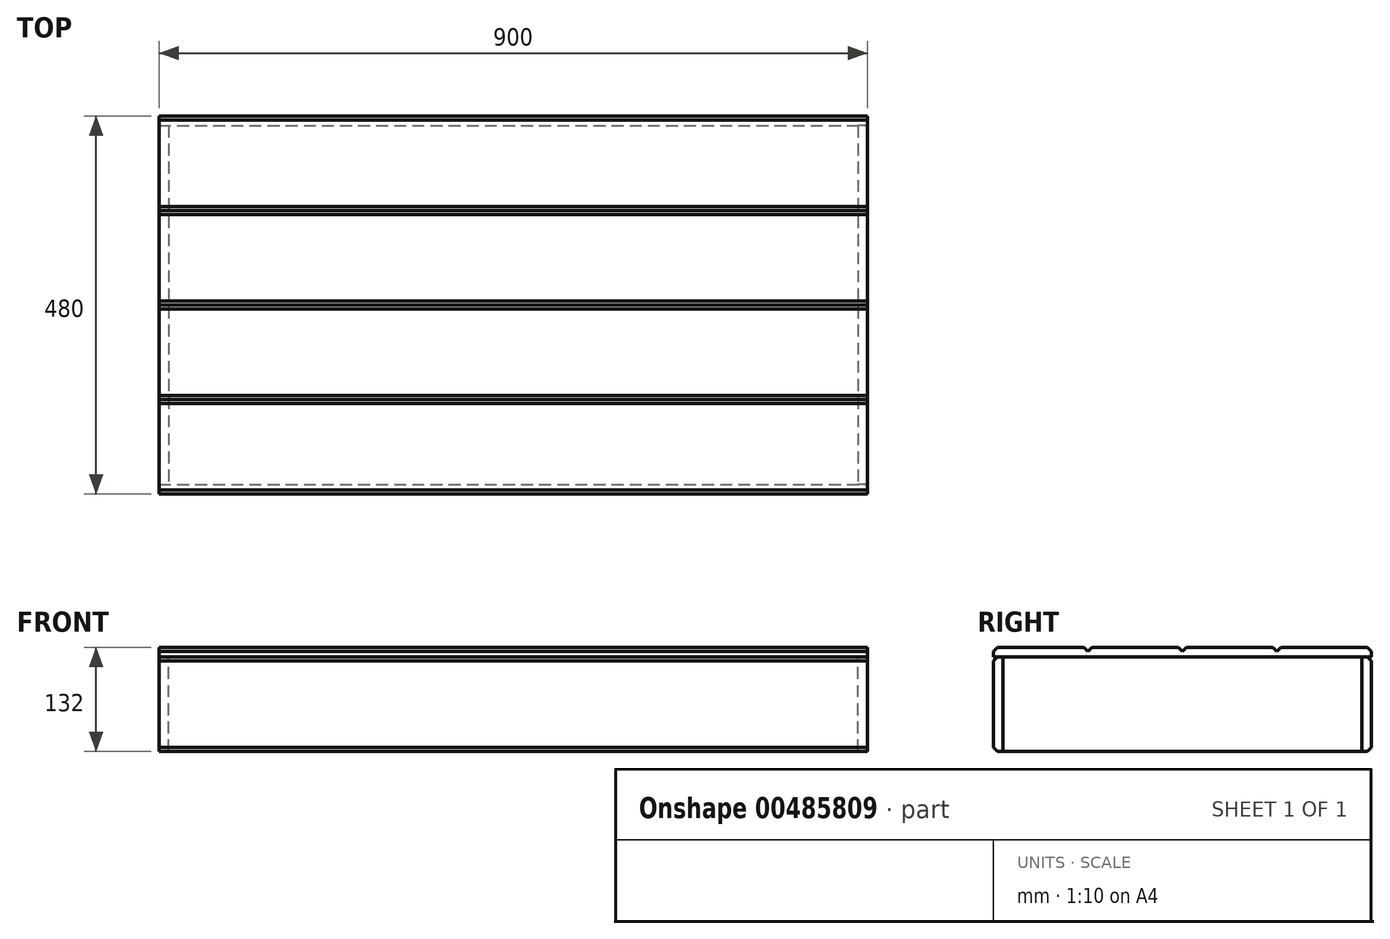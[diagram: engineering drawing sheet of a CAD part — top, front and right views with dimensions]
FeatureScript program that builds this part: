
annotation { "Feature Type Name" : "Feature", "Feature Type Description" : "" }
export const myFeature = defineFeature(function(context is Context, id is Id, definition is map)
    precondition{}
    {
        {
            var Q0;
            Q0=qCreatedBy(makeId("Top.planeOp"),FACE);
            var sketch = newSketch(context, id + "F0", { "sketchPlane" : qUnion([Q0])});
            skLineSegment(sketch, "E0", {"start": v(-56.43, 473.78) * mm, "end": v(-56.43, -6.22) * mm});
            skLineSegment(sketch, "E1", {"start": v(-56.43, -6.22) * mm, "end": v(843.57, -6.22) * mm});
            skLineSegment(sketch, "E2", {"start": v(-56.43, 473.78) * mm, "end": v(843.57, 473.78) * mm});
            skLineSegment(sketch, "E3", {"start": v(843.57, 473.78) * mm, "end": v(843.57, -6.22) * mm});
            skSolve(sketch);
        }
        {
            var Q0;
            Q0=makeQuery(id+"F0.imprint","IMPRINT",FACE,{"disambiguationData":[TD([[makeQuery(id+"F0.imprint","IMPRINT",EDGE,{"derivedFrom":sQuery(id+"F0.wireOp",EDGE,"E0")}),1.0]])]});
            extrude(context, id + "F1", {"entities" : qUnion([Q0]), "depth" : 12 * mm});
        }
        {
            var Q0;
            Q0=makeQuery(id+"F1.opExtrude","SWEPT_FACE",FACE,{"disambiguationData":[OSD([sQuery(id+"F0.wireOp",EDGE,"E3")])]});
            var sketch = newSketch(context, id + "F2", { "sketchPlane" : qUnion([Q0])});
            skLineSegment(sketch, "E4", {"start": v(-6.22, 12) * mm, "end": v(-1.22, 12) * mm});
            skLineSegment(sketch, "E5", {"start": v(-1.22, 12) * mm, "end": v(-6.22, 7) * mm});
            skLineSegment(sketch, "E6", {"start": v(-6.22, 7) * mm, "end": v(-6.22, 12) * mm});
            skLineSegment(sketch, "E7", {"start": v(-6.22, 18.21) * mm, "end": v(113.78, 18.21) * mm, "construction": true});
            skLineSegment(sketch, "E8", {"start": v(113.78, 12) * mm, "end": v(108.78, 12) * mm});
            skLineSegment(sketch, "E9", {"start": v(108.78, 12) * mm, "end": v(113.78, 7) * mm});
            skLineSegment(sketch, "E10", {"start": v(113.78, 7) * mm, "end": v(118.78, 12) * mm});
            skLineSegment(sketch, "E11", {"start": v(118.78, 12) * mm, "end": v(113.78, 12) * mm});
            skLineSegment(sketch, "E12", {"start": v(113.78, 18.21) * mm, "end": v(233.78, 18.21) * mm, "construction": true});
            skLineSegment(sketch, "E13", {"start": v(233.78, 18.21) * mm, "end": v(353.78, 18.21) * mm, "construction": true});
            skLineSegment(sketch, "E14", {"start": v(353.78, 18.21) * mm, "end": v(473.78, 18.21) * mm, "construction": true});
            skLineSegment(sketch, "E15", {"start": v(233.78, 12) * mm, "end": v(228.78, 12) * mm});
            skLineSegment(sketch, "E16", {"start": v(228.78, 12) * mm, "end": v(233.78, 7) * mm});
            skLineSegment(sketch, "E17", {"start": v(233.78, 7) * mm, "end": v(238.78, 12) * mm});
            skLineSegment(sketch, "E18", {"start": v(238.78, 12) * mm, "end": v(233.78, 12) * mm});
            skLineSegment(sketch, "E19", {"start": v(353.78, 12) * mm, "end": v(348.78, 12) * mm});
            skLineSegment(sketch, "E20", {"start": v(348.78, 12) * mm, "end": v(353.78, 7) * mm});
            skLineSegment(sketch, "E21", {"start": v(353.78, 7) * mm, "end": v(358.78, 12) * mm});
            skLineSegment(sketch, "E22", {"start": v(358.78, 12) * mm, "end": v(353.78, 12) * mm});
            skLineSegment(sketch, "E23", {"start": v(473.78, 12) * mm, "end": v(468.78, 12) * mm});
            skLineSegment(sketch, "E24", {"start": v(473.78, 12) * mm, "end": v(473.78, 7) * mm});
            skLineSegment(sketch, "E25", {"start": v(473.78, 7) * mm, "end": v(468.78, 12) * mm});
            skSolve(sketch);
        }
        {
            var Q0;
            Q0 = qSketchRegion(id + "F2", true);
            extrude(context, id + "F3", {"entities" : qUnion([Q0]), "operationType" : NewBodyOperationType.REMOVE, "endBound" : BoundingType.THROUGH_ALL, "oppositeDirection" : true, "depth" : 900 * mm});
        }
        {
            var Q0;
            Q0=makeQuery(id+"F1.opExtrude","CAP_FACE",FACE,{"disambiguationData":[OSD([sQuery(id+"F0.wireOp",EDGE,"E0"),sQuery(id+"F0.wireOp",EDGE,"E1"),sQuery(id+"F0.wireOp",EDGE,"E2"),sQuery(id+"F0.wireOp",EDGE,"E3")])],"isStart":true});
            var sketch = newSketch(context, id + "F4", { "sketchPlane" : qUnion([Q0])});
            skLineSegment(sketch, "E26.bottom", {"start": v(-56.43, -473.78) * mm, "end": v(843.57, -473.78) * mm});
            skLineSegment(sketch, "E26.top", {"start": v(-56.43, -461.78) * mm, "end": v(843.57, -461.78) * mm});
            skLineSegment(sketch, "E26.left", {"start": v(-56.43, -473.78) * mm, "end": v(-56.43, -461.78) * mm});
            skLineSegment(sketch, "E26.right", {"start": v(843.57, -473.78) * mm, "end": v(843.57, -461.78) * mm});
            skSolve(sketch);
        }
        {
            var Q0;
            Q0 = qSketchRegion(id + "F4", true);
            extrude(context, id + "F5", {"entities" : qUnion([Q0]), "depth" : 120 * mm});
        }
        {
            var Q0;
            Q0=makeQuery(id+"F1.opExtrude","CAP_FACE",FACE,{"disambiguationData":[OSD([sQuery(id+"F0.wireOp",EDGE,"E0"),sQuery(id+"F0.wireOp",EDGE,"E1"),sQuery(id+"F0.wireOp",EDGE,"E2"),sQuery(id+"F0.wireOp",EDGE,"E3")])],"isStart":true});
            var sketch = newSketch(context, id + "F6", { "sketchPlane" : qUnion([Q0])});
            skLineSegment(sketch, "E27.bottom", {"start": v(-56.43, 6.22) * mm, "end": v(843.57, 6.22) * mm});
            skLineSegment(sketch, "E27.top", {"start": v(-56.43, -5.78) * mm, "end": v(843.57, -5.78) * mm});
            skLineSegment(sketch, "E27.left", {"start": v(-56.43, 6.22) * mm, "end": v(-56.43, -5.78) * mm});
            skLineSegment(sketch, "E27.right", {"start": v(843.57, 6.22) * mm, "end": v(843.57, -5.78) * mm});
            skSolve(sketch);
        }
        {
            var Q0;
            Q0 = qSketchRegion(id + "F6", true);
            extrude(context, id + "F7", {"entities" : qUnion([Q0]), "depth" : 120 * mm});
        }
        {
            var Q0;
            Q0=makeQuery(id+"F1.opExtrude","CAP_FACE",FACE,{"disambiguationData":[OSD([sQuery(id+"F0.wireOp",EDGE,"E0"),sQuery(id+"F0.wireOp",EDGE,"E1"),sQuery(id+"F0.wireOp",EDGE,"E2"),sQuery(id+"F0.wireOp",EDGE,"E3")])],"isStart":true});
            var sketch = newSketch(context, id + "F8", { "sketchPlane" : qUnion([Q0])});
            skLineSegment(sketch, "E28", {"start": v(-96, 6.22) * mm, "end": v(-96, -5.78) * mm, "construction": true});
            skLineSegment(sketch, "E29", {"start": v(-56.43, -473.78) * mm, "end": v(-120.9, -473.78) * mm});
            skLineSegment(sketch, "E30", {"start": v(-120.9, -473.78) * mm, "end": v(-120.9, -461.78) * mm});
            skLineSegment(sketch, "E31.bottom", {"start": v(-56.43, -461.78) * mm, "end": v(-44.43, -461.78) * mm});
            skLineSegment(sketch, "E31.top", {"start": v(-56.43, -5.78) * mm, "end": v(-44.43, -5.78) * mm});
            skLineSegment(sketch, "E31.left", {"start": v(-56.43, -461.78) * mm, "end": v(-56.43, -5.78) * mm});
            skLineSegment(sketch, "E31.right", {"start": v(-44.43, -461.78) * mm, "end": v(-44.43, -5.78) * mm});
            skSolve(sketch);
        }
        {
            var Q0;
            Q0 = qSketchRegion(id + "F8", true);
            extrude(context, id + "F9", {"entities" : qUnion([Q0]), "depth" : 120 * mm});
        }
        {
            var Q0;
            Q0=makeQuery(id+"F1.opExtrude","CAP_FACE",FACE,{"disambiguationData":[OSD([sQuery(id+"F0.wireOp",EDGE,"E0"),sQuery(id+"F0.wireOp",EDGE,"E1"),sQuery(id+"F0.wireOp",EDGE,"E2"),sQuery(id+"F0.wireOp",EDGE,"E3")])],"isStart":true});
            var sketch = newSketch(context, id + "F10", { "sketchPlane" : qUnion([Q0])});
            skLineSegment(sketch, "E32", {"start": v(843.57, 6.22) * mm, "end": v(926.72, 6.22) * mm, "construction": true});
            skLineSegment(sketch, "E33", {"start": v(926.72, 6.22) * mm, "end": v(926.72, -5.78) * mm, "construction": true});
            skLineSegment(sketch, "E34", {"start": v(843.57, -473.78) * mm, "end": v(946.21, -473.78) * mm});
            skLineSegment(sketch, "E35", {"start": v(946.21, -473.78) * mm, "end": v(946.21, -461.78) * mm});
            skLineSegment(sketch, "E36.bottom", {"start": v(843.57, -461.78) * mm, "end": v(831.57, -461.78) * mm});
            skLineSegment(sketch, "E36.top", {"start": v(843.57, -5.78) * mm, "end": v(831.57, -5.78) * mm});
            skLineSegment(sketch, "E36.left", {"start": v(843.57, -461.78) * mm, "end": v(843.57, -5.78) * mm});
            skLineSegment(sketch, "E36.right", {"start": v(831.57, -461.78) * mm, "end": v(831.57, -5.78) * mm});
            skSolve(sketch);
        }
        {
            var Q0;
            Q0 = qSketchRegion(id + "F10", true);
            extrude(context, id + "F11", {"entities" : qUnion([Q0]), "depth" : 120 * mm});
        }
        {
            var Q0;
            Q0=makeQuery(id+"F7.opExtrude","SWEPT_FACE",FACE,{"disambiguationData":[OSD([sQuery(id+"F6.wireOp",EDGE,"E27.right")])]});
            var sketch = newSketch(context, id + "F12", { "sketchPlane" : qUnion([Q0])});
            skLineSegment(sketch, "E37", {"start": v(-6.22, 0) * mm, "end": v(-6.22, -5) * mm});
            skLineSegment(sketch, "E38", {"start": v(-6.22, -5) * mm, "end": v(-1.22, 0) * mm});
            skLineSegment(sketch, "E39", {"start": v(-1.22, 0) * mm, "end": v(-6.22, 0) * mm});
            skLineSegment(sketch, "E40", {"start": v(-6.22, -120) * mm, "end": v(-6.22, -115) * mm});
            skLineSegment(sketch, "E41", {"start": v(-6.22, -115) * mm, "end": v(-1.22, -120) * mm});
            skLineSegment(sketch, "E42", {"start": v(-1.22, -120) * mm, "end": v(-6.22, -120) * mm});
            skSolve(sketch);
        }
        {
            var Q0;
            Q0 = qSketchRegion(id + "F12", true);
            extrude(context, id + "F13", {"entities" : qUnion([Q0]), "operationType" : NewBodyOperationType.REMOVE, "endBound" : BoundingType.THROUGH_ALL, "oppositeDirection" : true, "depth" : 25 * mm});
        }
        {
            var Q0;
            Q0=makeQuery(id+"F5.opExtrude","SWEPT_FACE",FACE,{"disambiguationData":[OSD([sQuery(id+"F4.wireOp",EDGE,"E26.left")])]});
            var sketch = newSketch(context, id + "F14", { "sketchPlane" : qUnion([Q0])});
            skLineSegment(sketch, "E43", {"start": v(-473.78, 0) * mm, "end": v(-468.78, 0) * mm});
            skPoint(sketch, "E43.endSnap0", {"position": v(-467.78, 0) * mm});
            skLineSegment(sketch, "E44", {"start": v(-468.78, 0) * mm, "end": v(-473.78, -5) * mm});
            skLineSegment(sketch, "E45", {"start": v(-473.78, -5) * mm, "end": v(-473.78, 0) * mm});
            skLineSegment(sketch, "E46", {"start": v(-473.78, -120) * mm, "end": v(-473.78, -115) * mm});
            skLineSegment(sketch, "E47", {"start": v(-473.78, -115) * mm, "end": v(-468.78, -120) * mm});
            skLineSegment(sketch, "E48", {"start": v(-468.78, -120) * mm, "end": v(-473.78, -120) * mm});
            skSolve(sketch);
        }
        {
            var Q0;
            Q0 = qSketchRegion(id + "F14", true);
            extrude(context, id + "F15", {"entities" : qUnion([Q0]), "operationType" : NewBodyOperationType.REMOVE, "endBound" : BoundingType.THROUGH_ALL, "oppositeDirection" : true, "depth" : 25 * mm});
        }
    });
